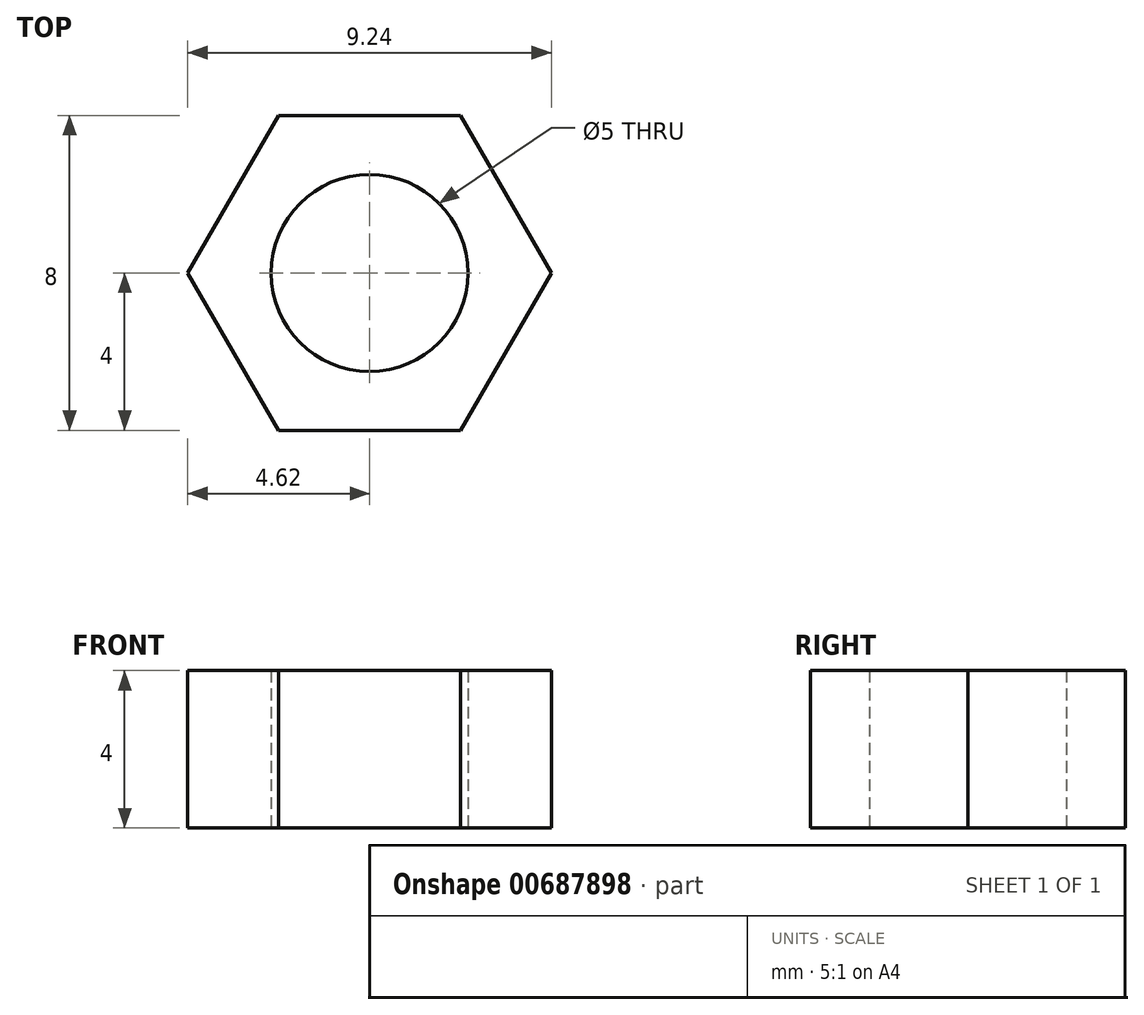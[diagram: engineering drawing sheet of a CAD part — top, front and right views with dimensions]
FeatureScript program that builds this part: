
annotation { "Feature Type Name" : "Feature", "Feature Type Description" : "" }
export const myFeature = defineFeature(function(context is Context, id is Id, definition is map)
    precondition{}
    {
        {
            var Q0;
            Q0=qCreatedBy(makeId("Top.planeOp"),FACE);
            var sketch = newSketch(context, id + "F0", { "sketchPlane" : qUnion([Q0])});
            skCircle(sketch, "E0.cCircle", {"center": v(0, 0) * mm, "radius": 4 * mm, "construction": true});
            skLineSegment(sketch, "E0.0", {"start": v(-2.3, 4) * mm, "end": v(2.3, 4) * mm});
            skLineSegment(sketch, "E0.1", {"start": v(2.3, 4) * mm, "end": v(4.62, 0) * mm});
            skLineSegment(sketch, "E0.2", {"start": v(4.62, 0) * mm, "end": v(2.3, -4) * mm});
            skLineSegment(sketch, "E0.3", {"start": v(2.3, -4) * mm, "end": v(-2.3, -4) * mm});
            skLineSegment(sketch, "E0.4", {"start": v(-2.3, -4) * mm, "end": v(-4.62, 0) * mm});
            skLineSegment(sketch, "E0.5", {"start": v(-4.62, 0) * mm, "end": v(-2.3, 4) * mm});
            skPoint(sketch, "E0.0.midPoint", {"position": v(0, 4) * mm});
            skCircle(sketch, "E1", {"center": v(0, 0) * mm, "radius": 2.5 * mm});
            skSolve(sketch);
        }
        {
            var Q0;
            Q0=makeQuery(id+"F0.imprint","IMPRINT",FACE,{"disambiguationData":[TD([[makeQuery(id+"F0.imprint","IMPRINT",EDGE,{"derivedFrom":sQuery(id+"F0.wireOp",EDGE,"E0.0")}),-1.0]])]});
            extrude(context, id + "F1", {"entities" : qUnion([Q0]), "depth" : 4 * mm, "offsetDistance" : 25 * mm});
        }
    });
